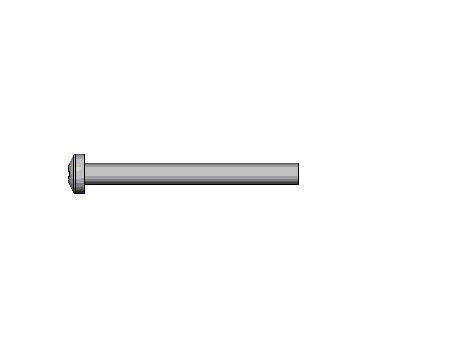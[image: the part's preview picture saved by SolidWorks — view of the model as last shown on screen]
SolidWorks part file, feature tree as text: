
SOLIDWORKS PART (.sldprt)
format: sldprt  version: not decoded by parser v0  size: 123,904 bytes
history: native  units: mm
features: plane x4, sketch x4, pattern_linear x4, revolve x1, thread x1, pattern_circular x1, cut_revolve x1 (+8 scaffold rows collapsed; 1 parser-record rows omitted)
feature tree (25):
  scaffold x8  (default folders/planes/origin — collapsed)
  plane  "Plane1"
  plane  "Plane2"
  plane  "Plane3"
  parser-record x1  (decoder bookkeeping rows leaked as tree rows — omitted from the tree; the rows remain in map.json)
  revolve  "Base-Revolve"  [1 undecoded]
  sketch  "BodySke"  dims[c1.Head_fillet_rad=3.6322mm c1.Head_crown_rad=5.0mm c2.Head_fillet_rad=0.36mm c2.D1=~7.099516mm c2.Head_ang=85.0deg c2.Oval_ht=2.3876mm c2.Head_ht=6.1976mm c2.Diameter=3.0mm c2.Length=76.2mm c2.Head_dia=20.0152mm c3.Head_dia=15.3924mm c3.Head_ht=8.509mm c3.Length=30.0mm c3.Head_side_ht=6.1722mm c4.Head_ht=5.1562mm c4.Head_dia=18.4912mm c5.Head_ht=2.4mm c5.Head_dia=5.6mm c5.Advance=0.5mm c5.Thread_nom=30.0mm c5.Thread_lim=~37.30625mm]
  thread  "ThreadCosmetic"  Diameter=29.5mm Thread_length=29.5mm Thread_minor=2.439mm Head_dia=5.6mm  [1 undecoded]
  sketch  "Sketch3"  dims[Cross_dia=2.9mm D1=1.45mm Cross_width=0.74mm D2=0.37mm]
  plane  "Plane4"  Offset=1.76mm Cross_depth=1.76mm
  sketch  "Sketch4"  dims[D1=0.37mm D2=0.37mm D3=0.185mm D4=0.185mm]
  pattern_circular  "CirPattern1"  Count=2 Angle=90deg
  sketch  "ThdSchSke"  dims[c1.Thread_minor=~1.03886mm c1.Diameter=~1.413535mm c1.Start=~0.988134mm c1.D4=~4.446753mm c1.Vee=60.0deg c2.Thread_minor=~1.03886mm c2.Start=~2.540025mm c2.D1=~0.108159mm c2.D2=~0.108159mm c3.D1=~0.216319mm c3.SideAngle=55.0deg c3.D2=~0.216319mm c3.VeeAngle=70.0deg c3.Thread_minor=2.439mm c3.Overcut=3.75mm c3.Diameter=3.0mm c3.D6=~8.326268mm c4.D1=~8.326268mm c5.D1=90.0deg c5.Start=11.1125mm c6.Start=~44.450025mm c7.Start=2.9mm]
  cut_revolve  "ThreadSchematic"  Angle=360deg
  pattern_linear  "ThdSchPat"  Count1=60 Count2=1 Spacing1=0.5mm Spacing2=50mm Num_threads=60 Advance=0.5mm
  pattern_linear  "ConfigurationName"  Spacing1=1 CopiedFlag=1  [1 undecoded]
  pattern_linear  "PartNumberID"  [2 undecoded]
  pattern_linear  "ConfigurationName"  Spacing1=0 CopiedFlag=0  [1 undecoded]
decode coverage: 10 of 12 modeling features carry decoded parameters
note: ~ marks probable driven/reference dimensions
note: 6 parameter values undecoded
note: suppression state not decoded; provenance and decode notes live in map.json
